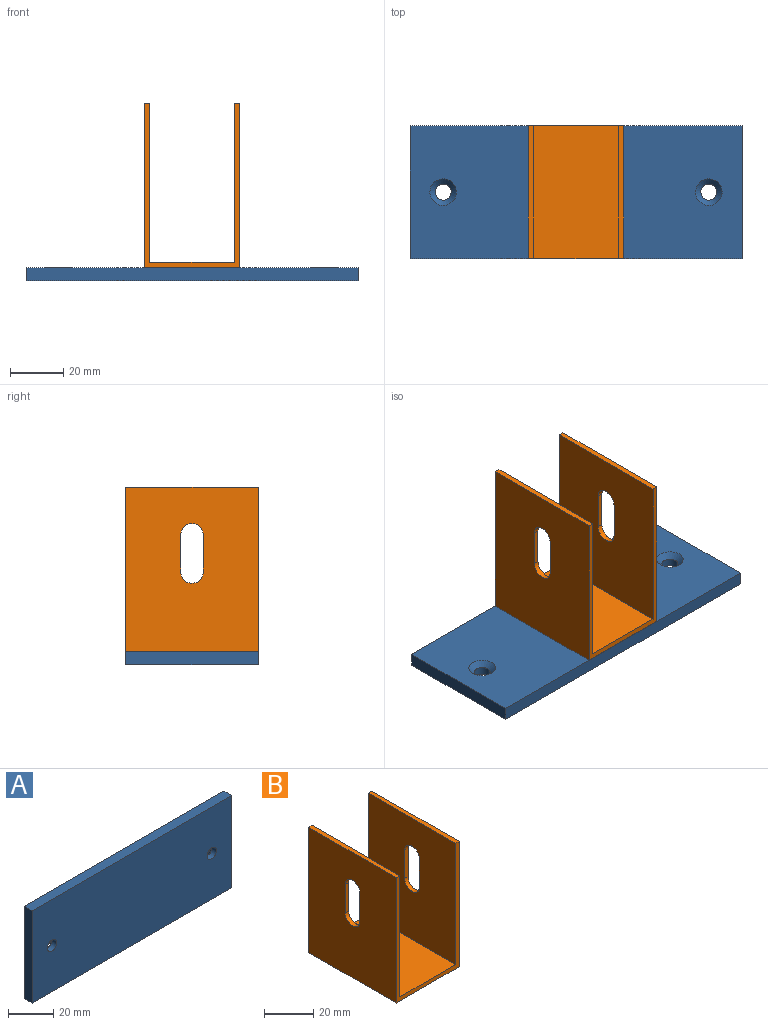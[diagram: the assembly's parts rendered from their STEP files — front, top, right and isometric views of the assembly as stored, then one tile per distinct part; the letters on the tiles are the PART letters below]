
ASSEMBLY  parts=2 mates=1
PART A: 10 faces, bbox 125x5x50 mm
  f0: plane 125x5mm, normal (0,0,-1), area 625mm2, adj f1,f3,f4,f5
  f1: plane 50x5mm, normal (1,0,0), area 250mm2, adj f0,f2,f4,f5
  f2: plane 125x5mm, normal (0,0,1), area 625mm2, adj f1,f3,f4,f5
  f3: plane 50x5mm, normal (-1,0,0), area 250mm2, adj f0,f2,f4,f5
  f4: plane 125x50mm, normal (0,-1,0), area 6193.5mm2, adj f0,f1,f2,f3,f6,f7
  f5: plane 125x50mm, normal (0,1,0), area 6092.9mm2, adj f0,f1,f2,f3,f8,f9
  f6: cylinder r=3mm len=6mm, axis (0,1,0), area 56.5mm2, adj f4,f8
  f7: cylinder r=3mm len=6mm, axis (0,1,0), area 56.5mm2, adj f4,f9
  f8: cone r=3mm half-angle=45deg, axis (0,1,0), area 71.1mm2, adj f5,f6
  f9: cone r=3mm half-angle=45deg, axis (0,1,0), area 71.1mm2, adj f5,f7
PART B: 18 faces, bbox 36x50x62 mm
  f0: plane 60x50mm, normal (1,0,0), area 2824.3mm2, adj f4,f5,f8,f9,f14,f15,f16,f17
  f1: plane 62x50mm, normal (-1,0,0), area 2924.3mm2, adj f5,f6,f8,f9,f14,f15,f16,f17
  f2: plane 62x50mm, normal (1,0,0), area 2924.3mm2, adj f6,f7,f8,f9,f10,f11,f12,f13
  f3: plane 60x50mm, normal (-1,0,0), area 2824.3mm2, adj f4,f7,f8,f9,f10,f11,f12,f13
  f4: plane 50x32mm, normal (0,0,1), area 1600mm2, adj f0,f3,f8,f9
  f5: plane 50x2mm, normal (0,0,1), area 100mm2, adj f0,f1,f8,f9
  f6: plane 50x36mm, normal (0,0,-1), area 1800mm2, adj f1,f2,f8,f9
  f7: plane 50x2mm, normal (0,0,1), area 100mm2, adj f2,f3,f8,f9
  f8: plane 62x36mm, normal (0,-1,0), area 312mm2, adj f0,f1,f2,f3,f4,f5,f6,f7
  f9: plane 62x36mm, normal (0,1,0), area 312mm2, adj f0,f1,f2,f3,f4,f5,f6,f7
  f10: cylinder r=4.25mm len=8.5mm, axis (1,0,0), area 26.7mm2, adj f2,f3,f11,f13
  f11: plane 14x2mm, normal (0,-1,0), area 28mm2, adj f2,f3,f10,f12
  f12: cylinder r=4.25mm len=8.5mm, axis (1,0,0), area 26.7mm2, adj f2,f3,f11,f13
  f13: plane 14x2mm, normal (0,1,0), area 28mm2, adj f2,f3,f10,f12
  f14: plane 14x2mm, normal (0,1,0), area 28mm2, adj f0,f1,f15,f17
  f15: cylinder r=4.25mm len=8.5mm, axis (1,0,0), area 26.7mm2, adj f0,f1,f14,f16
  f16: plane 14x2mm, normal (0,-1,0), area 28mm2, adj f0,f1,f15,f17
  f17: cylinder r=4.25mm len=8.5mm, axis (1,0,0), area 26.7mm2, adj f0,f1,f14,f16
PLACE A rot(axis=(1,0,0),90deg) t=(16,-25,-2)mm
PLACE B t=(0,0,5)mm
MATE fastened B.f6 <-> A.f5  axis (0,0,-1) through (16,-25,3)mm
